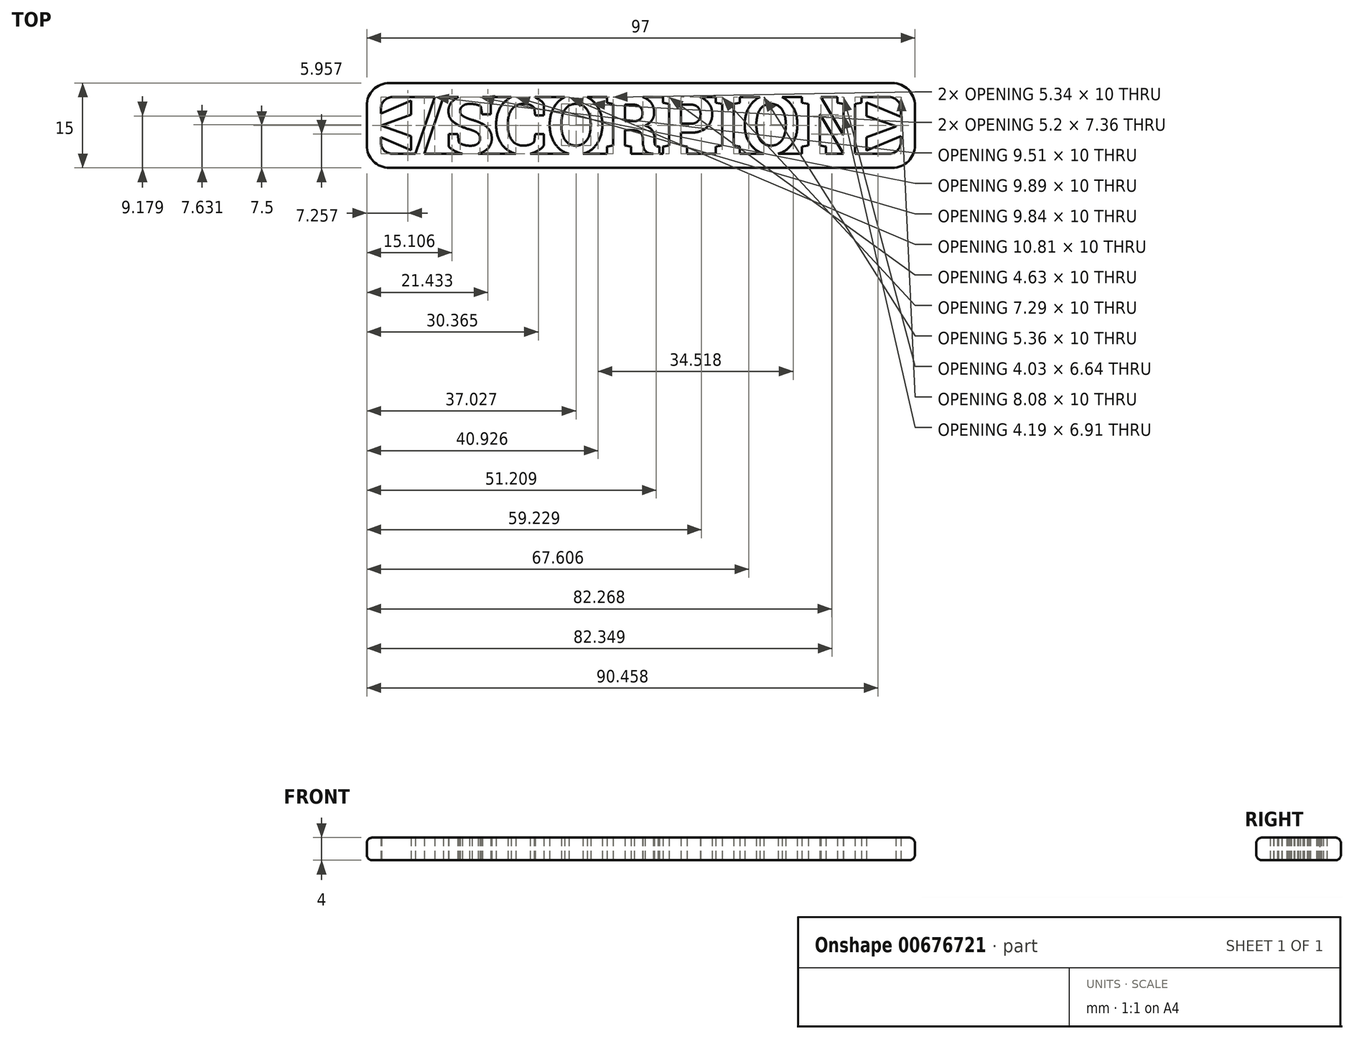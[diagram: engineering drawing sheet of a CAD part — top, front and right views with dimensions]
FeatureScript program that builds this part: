
annotation { "Feature Type Name" : "Feature", "Feature Type Description" : "" }
export const myFeature = defineFeature(function(context is Context, id is Id, definition is map)
    precondition{}
    {
        {
            var Q0;
            Q0=qCreatedBy(makeId("Top.planeOp"),FACE);
            var sketch = newSketch(context, id + "F0", { "sketchPlane" : qUnion([Q0])});
            skText(sketch, "E0", { "text": "/SCORPION", "fontName": "RobotoSlab-Bold.ttf"});
            skText(sketch, "E1", { "text": "<", "fontName": "RobotoSlab-Bold.ttf"});
            skText(sketch, "E2", { "text": ">", "fontName": "RobotoSlab-Bold.ttf"});
            skLineSegment(sketch, "E3.bottom", {"start": v(-46, 10) * mm, "end": v(46, 10) * mm});
            skLineSegment(sketch, "E3.top", {"start": v(-46, 0) * mm, "end": v(46, 0) * mm});
            skLineSegment(sketch, "E3.left", {"start": v(-46, 10) * mm, "end": v(-46, 0) * mm});
            skLineSegment(sketch, "E3.right", {"start": v(46, 10) * mm, "end": v(46, 0) * mm});
            skLineSegment(sketch, "E4.0", {"start": v(-48.5, 12.5) * mm, "end": v(48.5, 12.5) * mm});
            skLineSegment(sketch, "E4.1", {"start": v(-48.5, 12.5) * mm, "end": v(-48.5, -2.5) * mm});
            skLineSegment(sketch, "E4.2", {"start": v(-48.5, -2.5) * mm, "end": v(48.5, -2.5) * mm});
            skLineSegment(sketch, "E4.3", {"start": v(48.5, 12.5) * mm, "end": v(48.5, -2.5) * mm});
            skLineSegment(sketch, "E5", {"start": v(0, -12.53) * mm, "end": v(0, 35.85) * mm, "construction": true});
            const initialGuessF0  = {"E0": [-0.04, 0, 1, 0, 0.0104], "E1": [-0.049, 0, 1, 0, 0.01342], "E2": [0.039, 0, 1, 0, 0.01313]};
            skSetInitialGuess(sketch, initialGuessF0);
            skSolve(sketch);
        }
        {
            var Q0;
            Q0=makeQuery(id+"F0.imprint","IMPRINT",FACE,{"disambiguationData":[TD([[makeQuery(id+"F0.imprint","IMPRINT",EDGE,{"derivedFrom":sQuery(id+"F0.wireOp",EDGE,"E1.sketch_text.stroke-0")}),-1.0]])]});
            var Q1;
            {var subQ0=sQuery(id+"F0.wireOp",EDGE,"E3.top");var subQ1=sQuery(id+"F0.wireOp",EDGE,"E0.sketch_text.stroke-1");var subQ2=makeQuery(id+"F0.imprint","INTERSECT",VERTEX,{"derivedFrom":[subQ1,subQ0]});Q1=makeQuery(id+"F0.imprint","IMPRINT",FACE,{"disambiguationData":[TD([[makeQuery(id+"F0.imprint","IMPRINT",EDGE,{"disambiguationData":[TD([[subQ2,-1.0]])],"derivedFrom":subQ1}),-1.0]])]});}
            var Q2;
            {var subQ28=sQuery(id+"F0.wireOp",EDGE,"E0.sketch_text.stroke-0");Q2=makeQuery(id+"F0.imprint","IMPRINT",FACE,{"disambiguationData":[TD([[makeQuery(id+"F0.imprint","IMPRINT",EDGE,{"derivedFrom":subQ28}),1.0]])]});}
            var Q3;
            {var subQ0=sQuery(id+"F0.wireOp",EDGE,"E1.sketch_text.stroke-4");Q3=makeQuery(id+"F0.imprint","IMPRINT",FACE,{"disambiguationData":[TD([[makeQuery(id+"F0.imprint","IMPRINT",EDGE,{"derivedFrom":subQ0}),-1.0]])]});}
            var Q4;
            {var subQ0=sQuery(id+"F0.wireOp",EDGE,"E0.sketch_text.stroke-0");Q4=makeQuery(id+"F0.imprint","IMPRINT",FACE,{"disambiguationData":[TD([[makeQuery(id+"F0.imprint","IMPRINT",EDGE,{"derivedFrom":subQ0}),-1.0]])]});}
            var Q5;
            {var subQ0=sQuery(id+"F0.wireOp",EDGE,"E0.sketch_text.stroke-2");Q5=makeQuery(id+"F0.imprint","IMPRINT",FACE,{"disambiguationData":[TD([[makeQuery(id+"F0.imprint","IMPRINT",EDGE,{"derivedFrom":subQ0}),-1.0]])]});}
            var Q6;
            {var subQ0=sQuery(id+"F0.wireOp",EDGE,"E0.sketch_text.stroke-31");Q6=makeQuery(id+"F0.imprint","IMPRINT",FACE,{"disambiguationData":[TD([[makeQuery(id+"F0.imprint","IMPRINT",EDGE,{"derivedFrom":subQ0}),-1.0]])]});}
            var Q7;
            Q7=makeQuery(id+"F0.imprint","IMPRINT",FACE,{"disambiguationData":[TD([[makeQuery(id+"F0.imprint","IMPRINT",EDGE,{"derivedFrom":sQuery(id+"F0.wireOp",EDGE,"E0.sketch_text.stroke-4")}),-1.0]])]});
            var Q8;
            {var subQ0=sQuery(id+"F0.wireOp",EDGE,"E0.sketch_text.stroke-55");var subQ1=sQuery(id+"F0.wireOp",EDGE,"E0.sketch_text.stroke-54");var subQ2=makeQuery(id+"F0.imprint","INTERSECT",VERTEX,{"derivedFrom":[subQ1,subQ0]});Q8=makeQuery(id+"F0.imprint","IMPRINT",FACE,{"disambiguationData":[TD([[makeQuery(id+"F0.imprint","IMPRINT",EDGE,{"disambiguationData":[TD([[subQ2,1.0]])],"derivedFrom":subQ1}),-1.0]])]});}
            var Q9;
            Q9=makeQuery(id+"F0.imprint","IMPRINT",FACE,{"disambiguationData":[TD([[makeQuery(id+"F0.imprint","IMPRINT",EDGE,{"derivedFrom":sQuery(id+"F0.wireOp",EDGE,"E0.sketch_text.stroke-34")}),-1.0]])]});
            var Q10;
            {var subQ0=sQuery(id+"F0.wireOp",EDGE,"E0.sketch_text.stroke-16");var subQ1=sQuery(id+"F0.wireOp",EDGE,"E0.sketch_text.stroke-15");var subQ2=makeQuery(id+"F0.imprint","INTERSECT",VERTEX,{"derivedFrom":[subQ1,subQ0]});Q10=makeQuery(id+"F0.imprint","IMPRINT",FACE,{"disambiguationData":[TD([[makeQuery(id+"F0.imprint","IMPRINT",EDGE,{"disambiguationData":[TD([[subQ2,1.0]])],"derivedFrom":subQ1}),-1.0]])]});}
            var Q11;
            {var subQ0=sQuery(id+"F0.wireOp",EDGE,"E0.sketch_text.stroke-50");var subQ1=sQuery(id+"F0.wireOp",EDGE,"E0.sketch_text.stroke-49");var subQ2=makeQuery(id+"F0.imprint","INTERSECT",VERTEX,{"derivedFrom":[subQ1,subQ0]});Q11=makeQuery(id+"F0.imprint","IMPRINT",FACE,{"disambiguationData":[TD([[makeQuery(id+"F0.imprint","IMPRINT",EDGE,{"disambiguationData":[TD([[subQ2,1.0]])],"derivedFrom":subQ1}),-1.0]])]});}
            var Q12;
            {var subQ0=sQuery(id+"F0.wireOp",EDGE,"E0.sketch_text.stroke-60");var subQ1=sQuery(id+"F0.wireOp",EDGE,"E0.sketch_text.stroke-59");var subQ2=makeQuery(id+"F0.imprint","INTERSECT",VERTEX,{"derivedFrom":[subQ1,subQ0]});Q12=makeQuery(id+"F0.imprint","IMPRINT",FACE,{"disambiguationData":[TD([[makeQuery(id+"F0.imprint","IMPRINT",EDGE,{"disambiguationData":[TD([[subQ2,1.0]])],"derivedFrom":subQ1}),-1.0]])]});}
            var Q13;
            {var subQ7=sQuery(id+"F0.wireOp",EDGE,"E0.sketch_text.stroke-58");Q13=makeQuery(id+"F0.imprint","IMPRINT",FACE,{"disambiguationData":[TD([[makeQuery(id+"F0.imprint","IMPRINT",EDGE,{"derivedFrom":subQ7}),-1.0]])]});}
            var Q14;
            {var subQ5=sQuery(id+"F0.wireOp",EDGE,"E0.sketch_text.stroke-79");Q14=makeQuery(id+"F0.imprint","IMPRINT",FACE,{"disambiguationData":[TD([[makeQuery(id+"F0.imprint","IMPRINT",EDGE,{"derivedFrom":subQ5}),-1.0]])]});}
            var Q15;
            {var subQ0=sQuery(id+"F0.wireOp",EDGE,"E0.sketch_text.stroke-65");var subQ1=sQuery(id+"F0.wireOp",EDGE,"E0.sketch_text.stroke-64");var subQ2=makeQuery(id+"F0.imprint","INTERSECT",VERTEX,{"derivedFrom":[subQ1,subQ0]});Q15=makeQuery(id+"F0.imprint","IMPRINT",FACE,{"disambiguationData":[TD([[makeQuery(id+"F0.imprint","IMPRINT",EDGE,{"disambiguationData":[TD([[subQ2,1.0]])],"derivedFrom":subQ1}),-1.0]])]});}
            var Q16;
            {var subQ0=sQuery(id+"F0.wireOp",EDGE,"E0.sketch_text.stroke-105");Q16=makeQuery(id+"F0.imprint","IMPRINT",FACE,{"disambiguationData":[TD([[makeQuery(id+"F0.imprint","IMPRINT",EDGE,{"derivedFrom":subQ0}),-1.0]])]});}
            var Q17;
            {var subQ0=sQuery(id+"F0.wireOp",EDGE,"E0.sketch_text.stroke-115");Q17=makeQuery(id+"F0.imprint","IMPRINT",FACE,{"disambiguationData":[TD([[makeQuery(id+"F0.imprint","IMPRINT",EDGE,{"derivedFrom":subQ0}),-1.0]])]});}
            var Q18;
            {var subQ1=sQuery(id+"F0.wireOp",EDGE,"E0.sketch_text.stroke-128");Q18=makeQuery(id+"F0.imprint","IMPRINT",FACE,{"disambiguationData":[TD([[makeQuery(id+"F0.imprint","IMPRINT",EDGE,{"derivedFrom":subQ1}),-1.0]])]});}
            var Q19;
            {var subQ0=sQuery(id+"F0.wireOp",EDGE,"E0.sketch_text.stroke-138");Q19=makeQuery(id+"F0.imprint","IMPRINT",FACE,{"disambiguationData":[TD([[makeQuery(id+"F0.imprint","IMPRINT",EDGE,{"derivedFrom":subQ0}),-1.0]])]});}
            var Q20;
            {var subQ4=sQuery(id+"F0.wireOp",EDGE,"E0.sketch_text.stroke-140");Q20=makeQuery(id+"F0.imprint","IMPRINT",FACE,{"disambiguationData":[TD([[makeQuery(id+"F0.imprint","IMPRINT",EDGE,{"derivedFrom":subQ4}),-1.0]])]});}
            var Q21;
            {var subQ7=sQuery(id+"F0.wireOp",EDGE,"E0.sketch_text.stroke-149");Q21=makeQuery(id+"F0.imprint","IMPRINT",FACE,{"disambiguationData":[TD([[makeQuery(id+"F0.imprint","IMPRINT",EDGE,{"derivedFrom":subQ7}),-1.0]])]});}
            var Q22;
            {var subQ0=sQuery(id+"F0.wireOp",EDGE,"E0.sketch_text.stroke-156");var subQ1=sQuery(id+"F0.wireOp",EDGE,"E0.sketch_text.stroke-155");var subQ2=makeQuery(id+"F0.imprint","INTERSECT",VERTEX,{"derivedFrom":[subQ1,subQ0]});Q22=makeQuery(id+"F0.imprint","IMPRINT",FACE,{"disambiguationData":[TD([[makeQuery(id+"F0.imprint","IMPRINT",EDGE,{"disambiguationData":[TD([[subQ2,1.0]])],"derivedFrom":subQ1}),-1.0]])]});}
            var Q23;
            {var subQ0=sQuery(id+"F0.wireOp",EDGE,"E0.sketch_text.stroke-151");var subQ1=sQuery(id+"F0.wireOp",EDGE,"E0.sketch_text.stroke-150");var subQ2=makeQuery(id+"F0.imprint","INTERSECT",VERTEX,{"derivedFrom":[subQ1,subQ0]});Q23=makeQuery(id+"F0.imprint","IMPRINT",FACE,{"disambiguationData":[TD([[makeQuery(id+"F0.imprint","IMPRINT",EDGE,{"disambiguationData":[TD([[subQ2,1.0]])],"derivedFrom":subQ1}),-1.0]])]});}
            var Q24;
            {var subQ5=sQuery(id+"F0.wireOp",EDGE,"E0.sketch_text.stroke-170");Q24=makeQuery(id+"F0.imprint","IMPRINT",FACE,{"disambiguationData":[TD([[makeQuery(id+"F0.imprint","IMPRINT",EDGE,{"derivedFrom":subQ5}),-1.0]])]});}
            var Q25;
            {var subQ6=sQuery(id+"F0.wireOp",EDGE,"E0.sketch_text.stroke-184");Q25=makeQuery(id+"F0.imprint","IMPRINT",FACE,{"disambiguationData":[TD([[makeQuery(id+"F0.imprint","IMPRINT",EDGE,{"derivedFrom":subQ6}),-1.0]])]});}
            var Q26;
            {var subQ1=sQuery(id+"F0.wireOp",EDGE,"E0.sketch_text.stroke-191");Q26=makeQuery(id+"F0.imprint","IMPRINT",FACE,{"disambiguationData":[TD([[makeQuery(id+"F0.imprint","IMPRINT",EDGE,{"derivedFrom":subQ1}),-1.0]])]});}
            var Q27;
            {var subQ0=sQuery(id+"F0.wireOp",EDGE,"E2.sketch_text.stroke-4");Q27=makeQuery(id+"F0.imprint","IMPRINT",FACE,{"disambiguationData":[TD([[makeQuery(id+"F0.imprint","IMPRINT",EDGE,{"derivedFrom":subQ0}),-1.0]])]});}
            var Q28;
            Q28=makeQuery(id+"F0.imprint","IMPRINT",FACE,{"disambiguationData":[TD([[makeQuery(id+"F0.imprint","IMPRINT",EDGE,{"derivedFrom":sQuery(id+"F0.wireOp",EDGE,"E2.sketch_text.stroke-0")}),-1.0]])]});
            extrude(context, id + "F1", {"entities" : qUnion([Q0, Q1, Q2, Q3, Q4, Q5, Q6, Q7, Q8, Q9, Q10, Q11, Q12, Q13, Q14, Q15, Q16, Q17, Q18, Q19, Q20, Q21, Q22, Q23, Q24, Q25, Q26, Q27, Q28]), "depth" : 4 * mm, "offsetDistance" : 25 * mm});
        }
        {
            var Q0;
            Q0=makeQuery(id+"F1.opExtrude","SWEPT_EDGE",EDGE,{"disambiguationData":[OSD([sQuery(id+"F0.wireOp",EDGE,"E4.0"),sQuery(id+"F0.wireOp",EDGE,"E4.1")])]});
            var Q1;
            Q1=makeQuery(id+"F1.opExtrude","SWEPT_EDGE",EDGE,{"disambiguationData":[OSD([sQuery(id+"F0.wireOp",EDGE,"E4.1"),sQuery(id+"F0.wireOp",EDGE,"E4.2")])]});
            var Q2;
            Q2=makeQuery(id+"F1.opExtrude","SWEPT_EDGE",EDGE,{"disambiguationData":[OSD([sQuery(id+"F0.wireOp",EDGE,"E4.2"),sQuery(id+"F0.wireOp",EDGE,"E4.3")])]});
            var Q3;
            Q3=makeQuery(id+"F1.opExtrude","SWEPT_EDGE",EDGE,{"disambiguationData":[OSD([sQuery(id+"F0.wireOp",EDGE,"E4.0"),sQuery(id+"F0.wireOp",EDGE,"E4.3")])]});
            fillet(context, id + "F2", {"entities" : qUnion([Q0, Q1, Q2, Q3]), "radius" : 4 * mm, "tangentPropagation" : true, "allowEdgeOverflow" : false});
        }
        {
            var Q0;
            Q0=makeQuery(id+"F1.opExtrude","SWEPT_EDGE",EDGE,{"disambiguationData":[OSD([sQuery(id+"F0.wireOp",EDGE,"E3.bottom"),sQuery(id+"F0.wireOp",EDGE,"E3.left")])]});
            var Q1;
            Q1=makeQuery(id+"F1.opExtrude","SWEPT_EDGE",EDGE,{"disambiguationData":[OSD([sQuery(id+"F0.wireOp",EDGE,"E3.top"),sQuery(id+"F0.wireOp",EDGE,"E3.left")])]});
            var Q2;
            Q2=makeQuery(id+"F1.opExtrude","SWEPT_EDGE",EDGE,{"disambiguationData":[OSD([sQuery(id+"F0.wireOp",EDGE,"E3.bottom"),sQuery(id+"F0.wireOp",EDGE,"E3.right")])]});
            var Q3;
            Q3=makeQuery(id+"F1.opExtrude","SWEPT_EDGE",EDGE,{"disambiguationData":[OSD([sQuery(id+"F0.wireOp",EDGE,"E3.top"),sQuery(id+"F0.wireOp",EDGE,"E3.right")])]});
            fillet(context, id + "F3", {"entities" : qUnion([Q0, Q1, Q2, Q3]), "radius" : 2 * mm, "tangentPropagation" : true, "allowEdgeOverflow" : false});
        }
        {
            var Q0;
            Q0=makeQuery(id+"F1.opExtrude","CAP_EDGE",EDGE,{"disambiguationData":[OSD([sQuery(id+"F0.wireOp",EDGE,"E4.2")])],"isStart":false});
            var Q1;
            Q1=makeQuery(id+"F1.opExtrude","CAP_EDGE",EDGE,{"disambiguationData":[OSD([sQuery(id+"F0.wireOp",EDGE,"E4.2")])],"isStart":true});
            fillet(context, id + "F4", {"entities" : qUnion([Q0, Q1]), "radius" : 1 * mm, "tangentPropagation" : true, "allowEdgeOverflow" : false});
        }
    });
